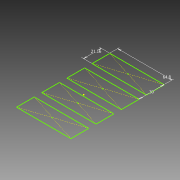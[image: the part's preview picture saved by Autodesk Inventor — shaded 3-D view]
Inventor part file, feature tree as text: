
AUTODESK INVENTOR PART (.ipt)
format: ipt  version: 2013 (Build 170138000, 138)  size: 84,480 bytes
history: native  units: mm
features: extrude x1, sketch x1
ambient origin geometry x8: Origin, YZ Plane, XZ Plane, XY Plane, X Axis, Y Axis, Z Axis, Center Point
bodies: Volumenkörper1 (feature_tree)
feature tree (2):
  extrude  "Extrusion1"  Depth=21.16mm
  sketch  "Skizze1"  dims[d0=64.8mm d2=21.16mm d3=40.0mm d5=30.0mm d6=10.0mm d8=10.0mm d10=0.17mm d11=0.0mm]
